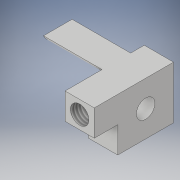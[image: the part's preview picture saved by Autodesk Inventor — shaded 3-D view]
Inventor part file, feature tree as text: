
AUTODESK INVENTOR PART (.ipt)
format: ipt  version: 2019 (Build 230136000, 136)  size: 147,456 bytes
history: native  units: in
note: dims shown in document units (in); Inventor stores cm internally (conversion verified against a paired STEP export)
features: sketch x5, extrude x4, hole x1, thread x1
ambient origin geometry x8: Origin, YZ Plane, XZ Plane, XY Plane, X Axis, Y Axis, Z Axis, Center Point
bodies: Solid1 (feature_tree)
feature tree (11):
  sketch  "Sketch1"  dims[d0=0.4488in d1=0.4764in]
  extrude  "Extrusion1"  Depth=0.4764in
  extrude  "Extrusion2"  Depth=0.1162in
  sketch  "Sketch3"  dims[d2=0.244in d3=0.1162in]
  sketch  "Sketch6"  dims[d4=0.25in d5=0.0in d6=0.5in d7=0.0in]
  hole  "Hole2"  [1 undecoded]
  extrude  "Extrusion8"  Depth=0.4764in
  sketch  "Sketch7"  dims[d19=0.4764in d20=0.2382in]
  extrude  "Extrusion9"  Depth=0.4488in
  thread  "Thread2"  [1 undecoded]
  sketch  "Sketch8"  dims[d29=0.0787in d30=0.4488in d31=0.2244in d33=0.4488in d37=0.1575in d38=0.75in d39=0.119in d40=0.25in d41=0.5635in d42=1.0in d43=0.8108in d46=0.2244in d47=0.2in d48=0.0in d50=0.25in d51=0.2244in d52=0.1122in d53=0.125in d63=0.1122in d64=0.125in d65=0.1575in d66=0.35in d67=0.0in d68=1.0in d69=0.0in d54=1.0in d55=1.0in d56=1.0in d57=0.15in d58=0.25in d59=0.375in d60=0.5635in d61=0.75in d62=0.8108in]
note: 2 required parameter values undecoded (feature->parameter linkage not recoverable at this tier; creation-order binding heuristic only, values carry confidence <= 0.55)
